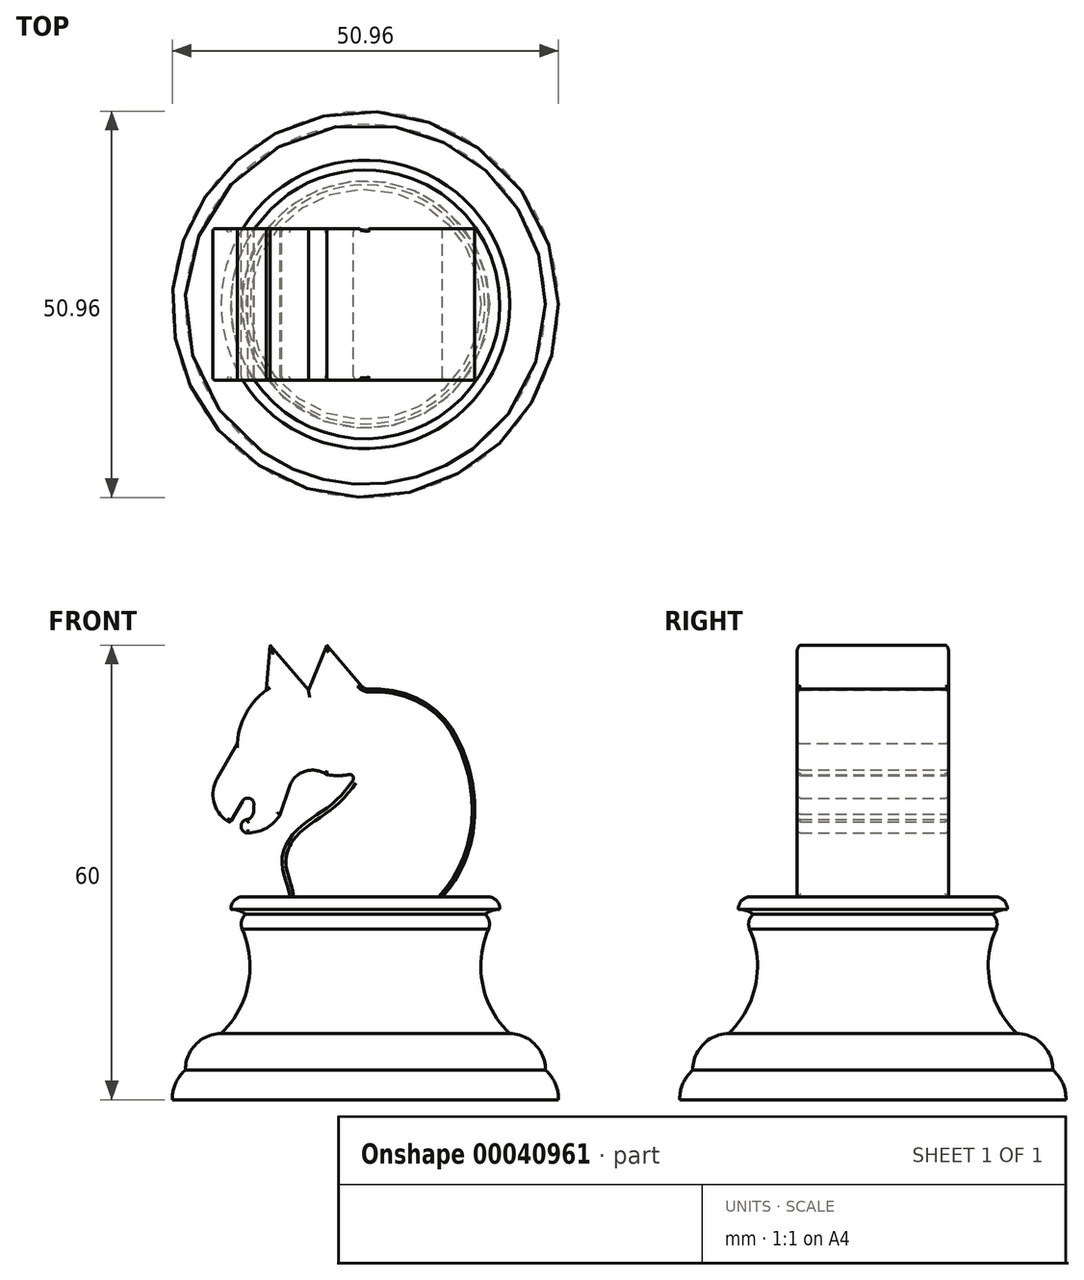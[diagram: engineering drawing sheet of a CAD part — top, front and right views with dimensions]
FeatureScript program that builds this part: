
annotation { "Feature Type Name" : "Feature", "Feature Type Description" : "" }
export const myFeature = defineFeature(function(context is Context, id is Id, definition is map)
    precondition{}
    {
        {
            var Q0;
            Q0=qCreatedBy(makeId("Front.planeOp"),FACE);
            var sketch = newSketch(context, id + "F0", { "sketchPlane" : qUnion([Q0])});
            skLineSegment(sketch, "E0", {"start": v(0, 33.2) * mm, "end": v(0, -26.8) * mm});
            skFitSpline(sketch, "E1", {"points": [v(10.13, 0) * mm, v(13.14, 18.7) * mm, v(6.04, 26.54) * mm, v(0, 27.26) * mm, v(0, 26.97) * mm], "startDerivative": vector(38.51, 42.5) * mm, "endDerivative": vector(3.44, -6.79) * mm});
            skLineSegment(sketch, "E2", {"start": v(0, 27.26) * mm, "end": v(-5.06, 33.2) * mm});
            skLineSegment(sketch, "E3", {"start": v(-5.06, 33.2) * mm, "end": v(-7.5, 27.26) * mm});
            skLineSegment(sketch, "E4", {"start": v(-7.5, 27.26) * mm, "end": v(-12.57, 33.2) * mm});
            skLineSegment(sketch, "E5", {"start": v(-12.57, 33.2) * mm, "end": v(-13.1, 27.26) * mm});
            skArc(sketch, "E6", {"start": v(-13.1, 27.26) * mm, "mid": v(-15.77, 24.2) * mm, "end": v(-16.88, 20.27) * mm});
            skLineSegment(sketch, "E7", {"start": v(-16.88, 20.27) * mm, "end": v(-19.74, 15.27) * mm});
            skLineSegment(sketch, "E8", {"start": v(-19.74, 15.27) * mm, "end": v(-21.64, 11.96) * mm});
            skLineSegment(sketch, "E9", {"start": v(-21.64, 11.96) * mm, "end": v(-17.84, 9.78) * mm});
            skLineSegment(sketch, "E10", {"start": v(-17.84, 9.78) * mm, "end": v(-16.21, 12.62) * mm});
            skArc(sketch, "E11", {"start": v(-14.8, 11.83) * mm, "mid": v(-15.12, 12.92) * mm, "end": v(-16.21, 12.62) * mm});
            skArc(sketch, "E12", {"start": v(-15.5, 10.2) * mm, "mid": v(-14.83, 10.88) * mm, "end": v(-14.8, 11.83) * mm});
            skArc(sketch, "E13", {"start": v(-15.5, 10.2) * mm, "mid": v(-16.4, 9.31) * mm, "end": v(-15.5, 8.42) * mm});
            skArc(sketch, "E14", {"start": v(-15.5, 8.42) * mm, "mid": v(-13.04, 9.1) * mm, "end": v(-11.21, 10.88) * mm});
            skPoint(sketch, "E14.endSnap0", {"position": v(-14.83, 10.88) * mm});
            skLineSegment(sketch, "E15", {"start": v(-11.21, 10.88) * mm, "end": v(-10.05, 14.5) * mm});
            skArc(sketch, "E16", {"start": v(-5.16, 16.14) * mm, "mid": v(-8.02, 16.55) * mm, "end": v(-10.05, 14.5) * mm});
            skArc(sketch, "E17", {"start": v(-5.16, 16.14) * mm, "mid": v(-2.94, 16.02) * mm, "end": v(-0.8, 16.55) * mm});
            skPoint(sketch, "E17.endSnap0", {"position": v(-8.02, 16.55) * mm});
            skFitSpline(sketch, "E18", {"points": [v(-0.8, 16.55) * mm, v(-4.5, 12.16) * mm, v(-8.87, 8.96) * mm, v(-11.02, 4.65) * mm, v(-10, 0) * mm], "startDerivative": vector(-16.07, -22.88) * mm, "endDerivative": vector(1.14, -17.56) * mm});
            skLineSegment(sketch, "E19", {"start": v(-10, 0) * mm, "end": v(10.13, 0) * mm});
            skLineSegment(sketch, "E20", {"start": v(0, 0) * mm, "end": v(-16.17, 0) * mm});
            skLineSegment(sketch, "E21", {"start": v(-1.02, 0) * mm, "end": v(-1.02, -26.8) * mm});
            skLineSegment(sketch, "E22", {"start": v(0, -26.8) * mm, "end": v(-1.02, -26.8) * mm});
            skArc(sketch, "E23", {"start": v(-19.03, -18.05) * mm, "mid": v(-15.47, -11.58) * mm, "end": v(-16.26, -4.24) * mm});
            skArc(sketch, "E24", {"start": v(-19.03, -18.05) * mm, "mid": v(-22.4, -19.5) * mm, "end": v(-23.75, -22.9) * mm});
            skArc(sketch, "E25", {"start": v(-23.75, -22.9) * mm, "mid": v(-25.06, -24.65) * mm, "end": v(-25.47, -26.8) * mm});
            skLineSegment(sketch, "E26", {"start": v(-25.47, -26.8) * mm, "end": v(-1.02, -26.8) * mm});
            skArc(sketch, "E27", {"start": v(-16.17, 0) * mm, "mid": v(-17.3, -0.5) * mm, "end": v(-17.73, -1.66) * mm});
            skArc(sketch, "E28", {"start": v(-15.78, -2.32) * mm, "mid": v(-16.7, -1.83) * mm, "end": v(-17.73, -1.66) * mm});
            skArc(sketch, "E29", {"start": v(-15.78, -2.32) * mm, "mid": v(-16.34, -3.2) * mm, "end": v(-16.26, -4.24) * mm});
            skSolve(sketch);
        }
        {
            var Q0;
            {var subQ1=sQuery(id+"F0.wireOp",EDGE,"E0");var subQ3=sQuery(id+"F0.wireOp",EDGE,"E1");var subQ6=makeQuery(id+"F0.imprint","INTERSECT",VERTEX,{"derivedFrom":[subQ1,subQ3]});Q0=makeQuery(id+"F0.imprint","IMPRINT",FACE,{"disambiguationData":[TD([[makeQuery(id+"F0.imprint","IMPRINT",EDGE,{"disambiguationData":[TD([[subQ6,-1.0]])],"derivedFrom":subQ1}),1.0]])]});}
            var Q1;
            {var subQ4=sQuery(id+"F0.wireOp",EDGE,"E2");Q1=makeQuery(id+"F0.imprint","IMPRINT",FACE,{"disambiguationData":[TD([[makeQuery(id+"F0.imprint","IMPRINT",EDGE,{"derivedFrom":subQ4}),1.0]])]});}
            var Q2;
            {var subQ0=sQuery(id+"F0.wireOp",EDGE,"E1");var subQ1=sQuery(id+"F0.wireOp",EDGE,"E0");var subQ3=makeQuery(id+"F0.imprint","INTERSECT",VERTEX,{"derivedFrom":[subQ1,subQ0]});Q2=makeQuery(id+"F0.imprint","IMPRINT",FACE,{"disambiguationData":[TD([[makeQuery(id+"F0.imprint","IMPRINT",EDGE,{"disambiguationData":[TD([[subQ3,1.0]])],"derivedFrom":subQ1}),-1.0]])]});}
            extrude(context, id + "F1", {"entities" : qUnion([Q0, Q1, Q2]), "endBound" : BoundingType.SYMMETRIC, "depth" : 20 * mm});
        }
        {
            var Q0;
            Q0=makeQuery(id+"F1.opExtrude","SWEPT_EDGE",EDGE,{"disambiguationData":[OSD([sQuery(id+"F0.wireOp",EDGE,"E8"),sQuery(id+"F0.wireOp",EDGE,"E9")])]});
            fillet(context, id + "F2", {"entities" : qUnion([Q0]), "radius" : 4.16 * mm, "tangentPropagation" : true, "allowEdgeOverflow" : false});
        }
        {
            var Q0;
            Q0=makeQuery(id+"F1.opExtrude","SWEPT_EDGE",EDGE,{"disambiguationData":[OSD([sQuery(id+"F0.wireOp",EDGE,"E11"),sQuery(id+"F0.wireOp",EDGE,"E12")])]});
            fillet(context, id + "F3", {"entities" : qUnion([Q0]), "radius" : 9.12 * mm, "tangentPropagation" : true, "allowEdgeOverflow" : false});
        }
        {
            var Q0;
            Q0=makeQuery(id+"F1.opExtrude","CAP_EDGE",EDGE,{"disambiguationData":[OSD([sQuery(id+"F0.wireOp",EDGE,"E12")])],"isStart":false});
            fillet(context, id + "F4", {"entities" : qUnion([Q0]), "radius" : 0.47 * mm, "tangentPropagation" : true, "allowEdgeOverflow" : false});
        }
        {
            var Q0;
            Q0=makeQuery(id+"F1.opExtrude","CAP_EDGE",EDGE,{"disambiguationData":[OSD([sQuery(id+"F0.wireOp",EDGE,"E13")])],"isStart":false});
            var Q1;
            Q1=makeQuery(id+"F1.opExtrude","CAP_EDGE",EDGE,{"disambiguationData":[OSD([sQuery(id+"F0.wireOp",EDGE,"E14")])],"isStart":false});
            var Q2;
            Q2=makeQuery(id+"F1.opExtrude","CAP_EDGE",EDGE,{"disambiguationData":[OSD([sQuery(id+"F0.wireOp",EDGE,"E15")])],"isStart":false});
            fillet(context, id + "F5", {"entities" : qUnion([Q0, Q1, Q2]), "radius" : 0.47 * mm, "tangentPropagation" : true, "allowEdgeOverflow" : false});
        }
        {
            var Q0;
            Q0=makeQuery(id+"F1.opExtrude","CAP_EDGE",EDGE,{"disambiguationData":[OSD([sQuery(id+"F0.wireOp",EDGE,"E13")])],"isStart":true});
            var Q1;
            Q1=makeQuery(id+"F1.opExtrude","CAP_EDGE",EDGE,{"disambiguationData":[OSD([sQuery(id+"F0.wireOp",EDGE,"E12")])],"isStart":true});
            var Q2;
            {var subQ0=sQuery(id+"F0.wireOp",EDGE,"E11");var subQ1=sQuery(id+"F0.wireOp",EDGE,"E12");Q2=makeQuery(id+"F3.opFillet","BLEND_EDGE",EDGE,{"blendedFrom":[makeQuery(id+"F1.opExtrude","SWEPT_EDGE",EDGE,{"disambiguationData":[OSD([subQ0,subQ1])]}),makeQuery(id+"F1.opExtrude","CAP_FACE",FACE,{"disambiguationData":[OSD([sQuery(id+"F0.wireOp",EDGE,"E1"),sQuery(id+"F0.wireOp",EDGE,"E2"),sQuery(id+"F0.wireOp",EDGE,"E3"),sQuery(id+"F0.wireOp",EDGE,"E4"),sQuery(id+"F0.wireOp",EDGE,"E5"),sQuery(id+"F0.wireOp",EDGE,"E6"),sQuery(id+"F0.wireOp",EDGE,"E7"),sQuery(id+"F0.wireOp",EDGE,"E8"),sQuery(id+"F0.wireOp",EDGE,"E9"),sQuery(id+"F0.wireOp",EDGE,"E10"),subQ0,subQ1,sQuery(id+"F0.wireOp",EDGE,"E13"),sQuery(id+"F0.wireOp",EDGE,"E14"),sQuery(id+"F0.wireOp",EDGE,"E15"),sQuery(id+"F0.wireOp",EDGE,"E16"),sQuery(id+"F0.wireOp",EDGE,"E17"),sQuery(id+"F0.wireOp",EDGE,"E18"),sQuery(id+"F0.wireOp",EDGE,"E19")])],"isStart":true})],"blendedInto":[makeQuery(id+"F1.opExtrude","CAP_FACE",FACE,{"disambiguationData":[OSD([sQuery(id+"F0.wireOp",EDGE,"E1"),sQuery(id+"F0.wireOp",EDGE,"E2"),sQuery(id+"F0.wireOp",EDGE,"E3"),sQuery(id+"F0.wireOp",EDGE,"E4"),sQuery(id+"F0.wireOp",EDGE,"E5"),sQuery(id+"F0.wireOp",EDGE,"E6"),sQuery(id+"F0.wireOp",EDGE,"E7"),sQuery(id+"F0.wireOp",EDGE,"E8"),sQuery(id+"F0.wireOp",EDGE,"E9"),sQuery(id+"F0.wireOp",EDGE,"E10"),subQ0,subQ1,sQuery(id+"F0.wireOp",EDGE,"E13"),sQuery(id+"F0.wireOp",EDGE,"E14"),sQuery(id+"F0.wireOp",EDGE,"E15"),sQuery(id+"F0.wireOp",EDGE,"E16"),sQuery(id+"F0.wireOp",EDGE,"E17"),sQuery(id+"F0.wireOp",EDGE,"E18"),sQuery(id+"F0.wireOp",EDGE,"E19")])],"isStart":true})]});}
            var Q3;
            Q3=makeQuery(id+"F1.opExtrude","CAP_EDGE",EDGE,{"disambiguationData":[OSD([sQuery(id+"F0.wireOp",EDGE,"E11")])],"isStart":true});
            var Q4;
            Q4=makeQuery(id+"F1.opExtrude","CAP_EDGE",EDGE,{"disambiguationData":[OSD([sQuery(id+"F0.wireOp",EDGE,"E10")])],"isStart":true});
            var Q5;
            Q5=makeQuery(id+"F1.opExtrude","CAP_EDGE",EDGE,{"disambiguationData":[OSD([sQuery(id+"F0.wireOp",EDGE,"E14")])],"isStart":true});
            var Q6;
            Q6=makeQuery(id+"F1.opExtrude","CAP_EDGE",EDGE,{"disambiguationData":[OSD([sQuery(id+"F0.wireOp",EDGE,"E15")])],"isStart":true});
            fillet(context, id + "F6", {"entities" : qUnion([Q0, Q1, Q2, Q3, Q4, Q5, Q6]), "radius" : 0.47 * mm, "tangentPropagation" : true, "allowEdgeOverflow" : false});
        }
        {
            var Q0;
            {var subQ0=sQuery(id+"F0.wireOp",EDGE,"E8");var subQ1=sQuery(id+"F0.wireOp",EDGE,"E9");Q0=makeQuery(id+"F2.opFillet","BLEND_EDGE",EDGE,{"blendedFrom":[makeQuery(id+"F1.opExtrude","SWEPT_EDGE",EDGE,{"disambiguationData":[OSD([subQ0,subQ1])]}),makeQuery(id+"F1.opExtrude","CAP_FACE",FACE,{"disambiguationData":[OSD([sQuery(id+"F0.wireOp",EDGE,"E1"),sQuery(id+"F0.wireOp",EDGE,"E2"),sQuery(id+"F0.wireOp",EDGE,"E3"),sQuery(id+"F0.wireOp",EDGE,"E4"),sQuery(id+"F0.wireOp",EDGE,"E5"),sQuery(id+"F0.wireOp",EDGE,"E6"),sQuery(id+"F0.wireOp",EDGE,"E7"),subQ0,subQ1,sQuery(id+"F0.wireOp",EDGE,"E10"),sQuery(id+"F0.wireOp",EDGE,"E11"),sQuery(id+"F0.wireOp",EDGE,"E12"),sQuery(id+"F0.wireOp",EDGE,"E13"),sQuery(id+"F0.wireOp",EDGE,"E14"),sQuery(id+"F0.wireOp",EDGE,"E15"),sQuery(id+"F0.wireOp",EDGE,"E16"),sQuery(id+"F0.wireOp",EDGE,"E17"),sQuery(id+"F0.wireOp",EDGE,"E18"),sQuery(id+"F0.wireOp",EDGE,"E19")])],"isStart":false})],"blendedInto":[makeQuery(id+"F1.opExtrude","CAP_FACE",FACE,{"disambiguationData":[OSD([sQuery(id+"F0.wireOp",EDGE,"E1"),sQuery(id+"F0.wireOp",EDGE,"E2"),sQuery(id+"F0.wireOp",EDGE,"E3"),sQuery(id+"F0.wireOp",EDGE,"E4"),sQuery(id+"F0.wireOp",EDGE,"E5"),sQuery(id+"F0.wireOp",EDGE,"E6"),sQuery(id+"F0.wireOp",EDGE,"E7"),subQ0,subQ1,sQuery(id+"F0.wireOp",EDGE,"E10"),sQuery(id+"F0.wireOp",EDGE,"E11"),sQuery(id+"F0.wireOp",EDGE,"E12"),sQuery(id+"F0.wireOp",EDGE,"E13"),sQuery(id+"F0.wireOp",EDGE,"E14"),sQuery(id+"F0.wireOp",EDGE,"E15"),sQuery(id+"F0.wireOp",EDGE,"E16"),sQuery(id+"F0.wireOp",EDGE,"E17"),sQuery(id+"F0.wireOp",EDGE,"E18"),sQuery(id+"F0.wireOp",EDGE,"E19")])],"isStart":false})]});}
            var Q1;
            {var subQ0=sQuery(id+"F0.wireOp",EDGE,"E8");var subQ1=sQuery(id+"F0.wireOp",EDGE,"E9");Q1=makeQuery(id+"F2.opFillet","BLEND_EDGE",EDGE,{"blendedFrom":[makeQuery(id+"F1.opExtrude","SWEPT_EDGE",EDGE,{"disambiguationData":[OSD([subQ0,subQ1])]}),makeQuery(id+"F1.opExtrude","CAP_FACE",FACE,{"disambiguationData":[OSD([sQuery(id+"F0.wireOp",EDGE,"E1"),sQuery(id+"F0.wireOp",EDGE,"E2"),sQuery(id+"F0.wireOp",EDGE,"E3"),sQuery(id+"F0.wireOp",EDGE,"E4"),sQuery(id+"F0.wireOp",EDGE,"E5"),sQuery(id+"F0.wireOp",EDGE,"E6"),sQuery(id+"F0.wireOp",EDGE,"E7"),subQ0,subQ1,sQuery(id+"F0.wireOp",EDGE,"E10"),sQuery(id+"F0.wireOp",EDGE,"E11"),sQuery(id+"F0.wireOp",EDGE,"E12"),sQuery(id+"F0.wireOp",EDGE,"E13"),sQuery(id+"F0.wireOp",EDGE,"E14"),sQuery(id+"F0.wireOp",EDGE,"E15"),sQuery(id+"F0.wireOp",EDGE,"E16"),sQuery(id+"F0.wireOp",EDGE,"E17"),sQuery(id+"F0.wireOp",EDGE,"E18"),sQuery(id+"F0.wireOp",EDGE,"E19")])],"isStart":true})],"blendedInto":[makeQuery(id+"F1.opExtrude","CAP_FACE",FACE,{"disambiguationData":[OSD([sQuery(id+"F0.wireOp",EDGE,"E1"),sQuery(id+"F0.wireOp",EDGE,"E2"),sQuery(id+"F0.wireOp",EDGE,"E3"),sQuery(id+"F0.wireOp",EDGE,"E4"),sQuery(id+"F0.wireOp",EDGE,"E5"),sQuery(id+"F0.wireOp",EDGE,"E6"),sQuery(id+"F0.wireOp",EDGE,"E7"),subQ0,subQ1,sQuery(id+"F0.wireOp",EDGE,"E10"),sQuery(id+"F0.wireOp",EDGE,"E11"),sQuery(id+"F0.wireOp",EDGE,"E12"),sQuery(id+"F0.wireOp",EDGE,"E13"),sQuery(id+"F0.wireOp",EDGE,"E14"),sQuery(id+"F0.wireOp",EDGE,"E15"),sQuery(id+"F0.wireOp",EDGE,"E16"),sQuery(id+"F0.wireOp",EDGE,"E17"),sQuery(id+"F0.wireOp",EDGE,"E18"),sQuery(id+"F0.wireOp",EDGE,"E19")])],"isStart":true})]});}
            fillet(context, id + "F7", {"entities" : qUnion([Q0, Q1]), "radius" : 0.3 * mm, "tangentPropagation" : true, "allowEdgeOverflow" : false});
        }
        {
            var Q0;
            Q0=makeQuery(id+"F1.opExtrude","SWEPT_FACE",FACE,{"disambiguationData":[OSD([sQuery(id+"F0.wireOp",EDGE,"E18")])]});
            var Q1;
            Q1=makeQuery(id+"F1.opExtrude","SWEPT_FACE",FACE,{"disambiguationData":[OSD([sQuery(id+"F0.wireOp",EDGE,"E17")])]});
            fillet(context, id + "F8", {"entities" : qUnion([Q0, Q1]), "radius" : 0.51 * mm, "tangentPropagation" : true, "allowEdgeOverflow" : false});
        }
        {
            var Q0;
            {var subQ1=sQuery(id+"F0.wireOp",EDGE,"E21");Q0=makeQuery(id+"F0.imprint","IMPRINT",FACE,{"disambiguationData":[TD([[makeQuery(id+"F0.imprint","IMPRINT",EDGE,{"derivedFrom":subQ1}),1.0]])]});}
            var Q1;
            {var subQ1=sQuery(id+"F0.wireOp",EDGE,"E21");Q1=makeQuery(id+"F0.imprint","IMPRINT",FACE,{"disambiguationData":[TD([[makeQuery(id+"F0.imprint","IMPRINT",EDGE,{"derivedFrom":subQ1}),-1.0]])]});}
            var Q2;
            Q2=sQuery(id+"F0.wireOp",EDGE,"E0");
            revolve(context, id + "F9", {"entities" : qUnion([Q0, Q1]), "axis" : qUnion([Q2]), "revolveType" : RevolveType.FULL});
        }
        {
            var Q0;
            Q0=makeQuery(id+"F1.opExtrude","CAP_EDGE",EDGE,{"disambiguationData":[OSD([sQuery(id+"F0.wireOp",EDGE,"E2")])],"isStart":false});
            var Q1;
            Q1=makeQuery(id+"F1.opExtrude","CAP_EDGE",EDGE,{"disambiguationData":[OSD([sQuery(id+"F0.wireOp",EDGE,"E3")])],"isStart":false});
            var Q2;
            Q2=makeQuery(id+"F1.opExtrude","CAP_EDGE",EDGE,{"disambiguationData":[OSD([sQuery(id+"F0.wireOp",EDGE,"E4")])],"isStart":false});
            var Q3;
            Q3=makeQuery(id+"F1.opExtrude","CAP_EDGE",EDGE,{"disambiguationData":[OSD([sQuery(id+"F0.wireOp",EDGE,"E5")])],"isStart":false});
            fillet(context, id + "F10", {"entities" : qUnion([Q0, Q1, Q2, Q3]), "radius" : 0.5 * mm, "tangentPropagation" : true, "allowEdgeOverflow" : false});
        }
        {
            var Q0;
            Q0=makeQuery(id+"F1.opExtrude","CAP_EDGE",EDGE,{"disambiguationData":[OSD([sQuery(id+"F0.wireOp",EDGE,"E5")])],"isStart":true});
            var Q1;
            Q1=makeQuery(id+"F1.opExtrude","CAP_EDGE",EDGE,{"disambiguationData":[OSD([sQuery(id+"F0.wireOp",EDGE,"E4")])],"isStart":true});
            var Q2;
            Q2=makeQuery(id+"F1.opExtrude","CAP_EDGE",EDGE,{"disambiguationData":[OSD([sQuery(id+"F0.wireOp",EDGE,"E3")])],"isStart":true});
            var Q3;
            Q3=makeQuery(id+"F1.opExtrude","CAP_EDGE",EDGE,{"disambiguationData":[OSD([sQuery(id+"F0.wireOp",EDGE,"E2")])],"isStart":true});
            fillet(context, id + "F11", {"entities" : qUnion([Q0, Q1, Q2, Q3]), "radius" : 0.47 * mm, "tangentPropagation" : true, "allowEdgeOverflow" : false});
        }
        {
            var Q0;
            Q0=makeQuery(id+"F1.opExtrude","SWEPT_EDGE",EDGE,{"disambiguationData":[OSD([sQuery(id+"F0.wireOp",EDGE,"E0"),sQuery(id+"F0.wireOp",EDGE,"E1"),sQuery(id+"F0.wireOp",EDGE,"E2")])]});
            fillet(context, id + "F12", {"entities" : qUnion([Q0]), "radius" : 1 * mm, "tangentPropagation" : true, "allowEdgeOverflow" : false});
        }
        {
            var Q0;
            Q0=makeQuery(id+"F1.opExtrude","CAP_EDGE",EDGE,{"disambiguationData":[OSD([sQuery(id+"F0.wireOp",EDGE,"E1")])],"isStart":true});
            var Q1;
            Q1=makeQuery(id+"F1.opExtrude","CAP_EDGE",EDGE,{"disambiguationData":[OSD([sQuery(id+"F0.wireOp",EDGE,"E1")])],"isStart":false});
            fillet(context, id + "F13", {"entities" : qUnion([Q0, Q1]), "radius" : 0.35 * mm, "tangentPropagation" : true, "allowEdgeOverflow" : false});
        }
    });
